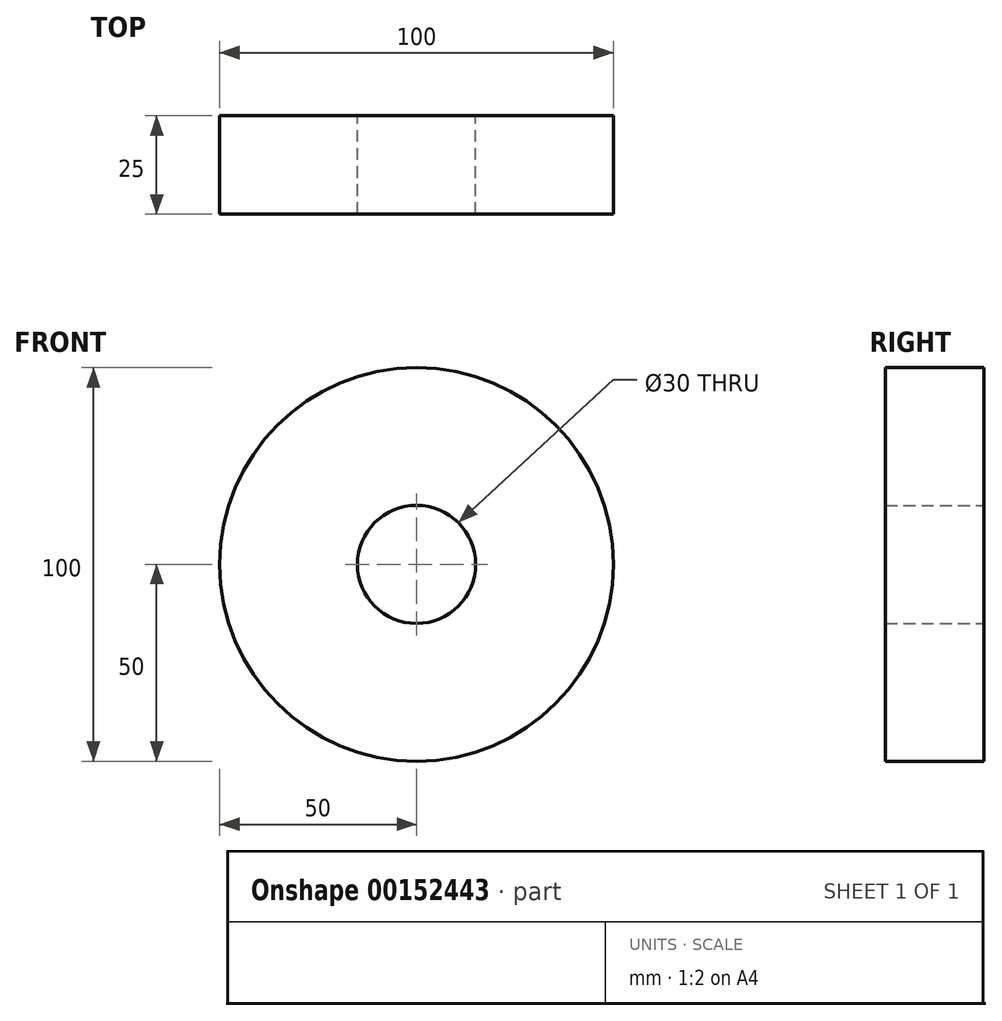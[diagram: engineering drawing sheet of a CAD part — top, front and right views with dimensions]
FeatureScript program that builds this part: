
annotation { "Feature Type Name" : "Feature", "Feature Type Description" : "" }
export const myFeature = defineFeature(function(context is Context, id is Id, definition is map)
    precondition{}
    {
        {
            var Q0;
            Q0=qCreatedBy(makeId("Front.planeOp"),FACE);
            var sketch = newSketch(context, id + "F0", { "sketchPlane" : qUnion([Q0])});
            skCircle(sketch, "E0", {"center": v(0, 0) * mm, "radius": 50 * mm});
            skCircle(sketch, "E1", {"center": v(0, 0) * mm, "radius": 15 * mm});
            skSolve(sketch);
        }
        {
            var Q0;
            Q0=makeQuery(id+"F0.imprint","IMPRINT",FACE,{"disambiguationData":[TD([[makeQuery(id+"F0.imprint","IMPRINT",EDGE,{"derivedFrom":sQuery(id+"F0.wireOp",EDGE,"E0")}),1.0]])]});
            extrude(context, id + "F1", {"entities" : qUnion([Q0]), "depth" : 25 * mm});
        }
        {
            var Q0;
            Q0=qCreatedBy(makeId("Right.planeOp"),FACE);
            cPlane(context, id + "F2", {"entities" : qUnion([Q0]), "cplaneType" : CPlaneType.OFFSET, "offset" : 50 * mm, "width" : 150 * mm, "height" : 150 * mm});
        }
        {
            var Q0;
            Q0=qCreatedBy(id+"F2.planeOp",FACE);
            var sketch = newSketch(context, id + "F3", { "sketchPlane" : qUnion([Q0])});
            skPoint(sketch, "E2", {"position": v(-12.5, 0) * mm});
            skCircle(sketch, "E3", {"center": v(-12.5, 0) * mm, "radius": 12.5 * mm});
            skSolve(sketch);
        }
        {
            var Q0;
            Q0=makeQuery(id+"F3.imprint","IMPRINT",FACE,{"disambiguationData":[TD([[makeQuery(id+"F3.imprint","IMPRINT",EDGE,{"derivedFrom":sQuery(id+"F3.wireOp",EDGE,"E3")}),1.0]])]});
            extrude(context, id + "F4", {"entities" : qUnion([Q0]), "operationType" : NewBodyOperationType.ADD, "depth" : 1000 * mm});
        }
        {
            var Q0;
            Q0=makeQuery(id+"F4.opExtrude","SWEPT_BODY",BODY,{"disambiguationData":[OSD([sQuery(id+"F3.wireOp",EDGE,"E3")])]});
            deleteBodies(context, id + "F5", {"entities" : qUnion([Q0])});
        }
    });
